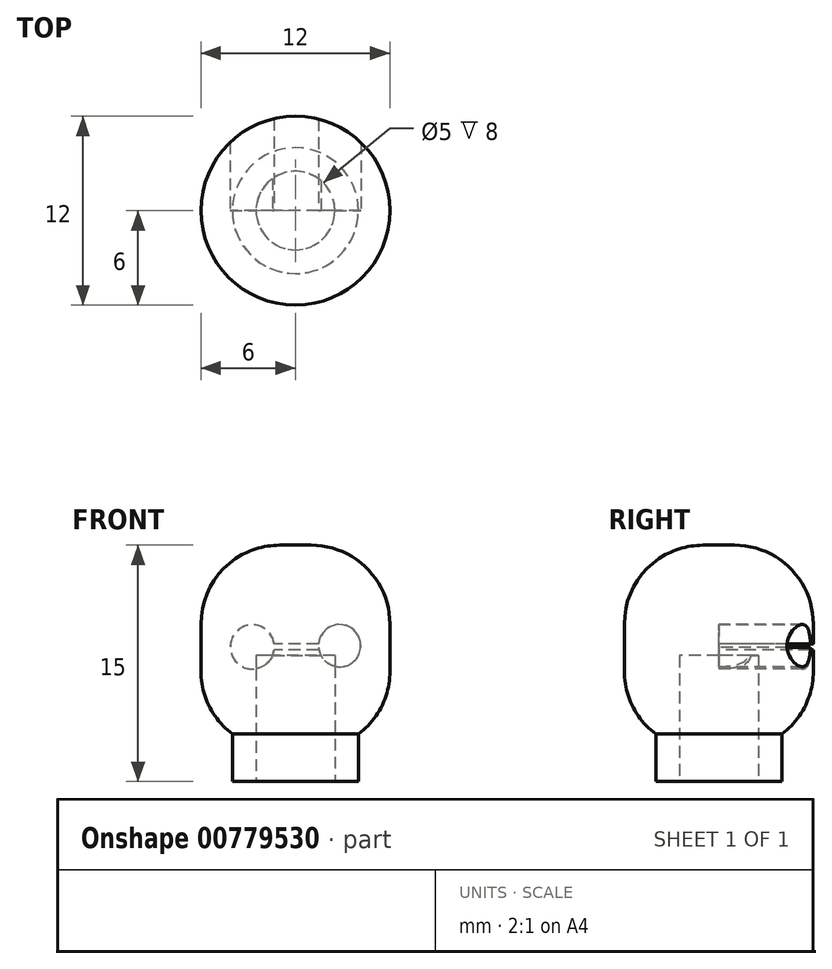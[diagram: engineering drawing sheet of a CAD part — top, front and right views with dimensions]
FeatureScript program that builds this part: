
annotation { "Feature Type Name" : "Feature", "Feature Type Description" : "" }
export const myFeature = defineFeature(function(context is Context, id is Id, definition is map)
    precondition{}
    {
        {
            var Q0;
            Q0=qCreatedBy(makeId("Top.planeOp"),FACE);
            var sketch = newSketch(context, id + "F0", { "sketchPlane" : qUnion([Q0])});
            skCircle(sketch, "E0", {"center": v(0, 0) * mm, "radius": 4 * mm});
            skSolve(sketch);
        }
        {
            var Q0;
            Q0 = qSketchRegion(id + "F0", true);
            extrude(context, id + "F1", {"entities" : qUnion([Q0]), "depth" : 3 * mm, "offsetDistance" : 25 * mm});
        }
        {
            var Q0;
            Q0=makeQuery(id+"F1.opExtrude","CAP_FACE",FACE,{"disambiguationData":[OSD([sQuery(id+"F0.wireOp",EDGE,"E0")])],"isStart":false});
            var sketch = newSketch(context, id + "F2", { "sketchPlane" : qUnion([Q0])});
            skCircle(sketch, "E1", {"center": v(0, 0) * mm, "radius": 6 * mm});
            skSolve(sketch);
        }
        {
            var Q0;
            Q0 = qSketchRegion(id + "F2", true);
            extrude(context, id + "F3", {"entities" : qUnion([Q0]), "operationType" : NewBodyOperationType.ADD, "depth" : 12 * mm, "offsetDistance" : 25 * mm});
        }
        {
            var Q0;
            Q0=makeQuery(id+"F3.opExtrude","CAP_FACE",FACE,{"disambiguationData":[OSD([sQuery(id+"F2.wireOp",EDGE,"E1")])],"isStart":false});
            fillet(context, id + "F4", {"entities" : qUnion([Q0]), "radius" : 5 * mm, "tangentPropagation" : true, "allowEdgeOverflow" : false});
        }
        {
            var Q0;
            Q0=makeQuery(id+"F3.opExtrude","CAP_EDGE",EDGE,{"disambiguationData":[OSD([sQuery(id+"F2.wireOp",EDGE,"E1")])],"isStart":true});
            fillet(context, id + "F5", {"entities" : qUnion([Q0]), "radius" : 5 * mm, "tangentPropagation" : true, "allowEdgeOverflow" : false});
        }
        {
            var Q0;
            Q0=makeQuery(id+"F1.opExtrude","CAP_FACE",FACE,{"disambiguationData":[OSD([sQuery(id+"F0.wireOp",EDGE,"E0")])],"isStart":true});
            var sketch = newSketch(context, id + "F6", { "sketchPlane" : qUnion([Q0])});
            skCircle(sketch, "E2", {"center": v(0, 0) * mm, "radius": 2.5 * mm});
            skSolve(sketch);
        }
        {
            var Q0;
            Q0 = qSketchRegion(id + "F6", true);
            extrude(context, id + "F7", {"entities" : qUnion([Q0]), "operationType" : NewBodyOperationType.REMOVE, "oppositeDirection" : true, "depth" : 8 * mm, "offsetDistance" : 25 * mm});
        }
        {
            var Q0;
            Q0=qCreatedBy(makeId("Front.planeOp"),FACE);
            var sketch = newSketch(context, id + "F8", { "sketchPlane" : qUnion([Q0])});
            skCircle(sketch, "E3", {"center": v(-2.74, 8.54) * mm, "radius": 1.4 * mm});
            skCircle(sketch, "E4", {"center": v(2.8, 8.62) * mm, "radius": 1.34 * mm});
            skLineSegment(sketch, "E5.bottom", {"start": v(1.47, 8.73) * mm, "end": v(-1.35, 8.73) * mm});
            skLineSegment(sketch, "E5.top", {"start": v(1.47, 8.35) * mm, "end": v(-1.35, 8.35) * mm});
            skLineSegment(sketch, "E5.left", {"start": v(1.47, 8.73) * mm, "end": v(1.47, 8.35) * mm});
            skLineSegment(sketch, "E5.right", {"start": v(-1.35, 8.73) * mm, "end": v(-1.35, 8.35) * mm});
            skSolve(sketch);
        }
        {
            var Q0;
            Q0 = qSketchRegion(id + "F8", true);
            extrude(context, id + "F9", {"entities" : qUnion([Q0]), "operationType" : NewBodyOperationType.REMOVE, "oppositeDirection" : true, "depth" : 8 * mm, "offsetDistance" : 25 * mm});
        }
    });
